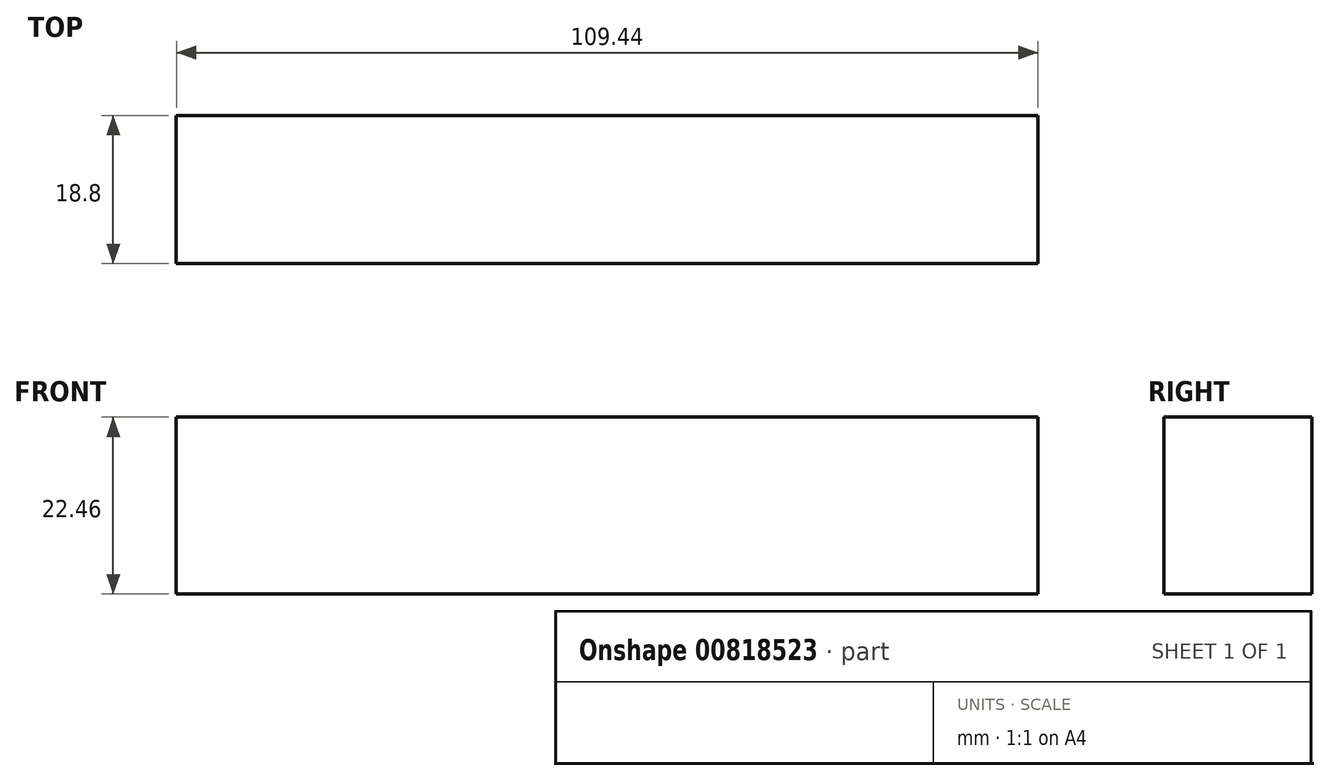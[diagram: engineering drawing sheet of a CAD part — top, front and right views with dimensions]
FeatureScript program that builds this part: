
annotation { "Feature Type Name" : "Feature", "Feature Type Description" : "" }
export const myFeature = defineFeature(function(context is Context, id is Id, definition is map)
    precondition{}
    {
        {
            var Q0;
            Q0=qCreatedBy(makeId("Front.planeOp"),FACE);
            var sketch = newSketch(context, id + "F0", { "sketchPlane" : qUnion([Q0])});
            skLineSegment(sketch, "E0.bottom", {"start": v(-54.72, 11.23) * mm, "end": v(54.72, 11.23) * mm});
            skLineSegment(sketch, "E0.top", {"start": v(-54.72, -11.23) * mm, "end": v(54.72, -11.23) * mm});
            skLineSegment(sketch, "E0.left", {"start": v(-54.72, 11.23) * mm, "end": v(-54.72, -11.23) * mm});
            skLineSegment(sketch, "E0.right", {"start": v(54.72, 11.23) * mm, "end": v(54.72, -11.23) * mm});
            skPoint(sketch, "E0.middle", {"position": v(0, 0) * mm});
            skSolve(sketch);
        }
        {
            var Q0;
            Q0 = qSketchRegion(id + "F0", true);
            extrude(context, id + "F1", {"entities" : qUnion([Q0]), "depth" : 18.8 * mm, "offsetDistance" : 25.4 * mm});
        }
    });
